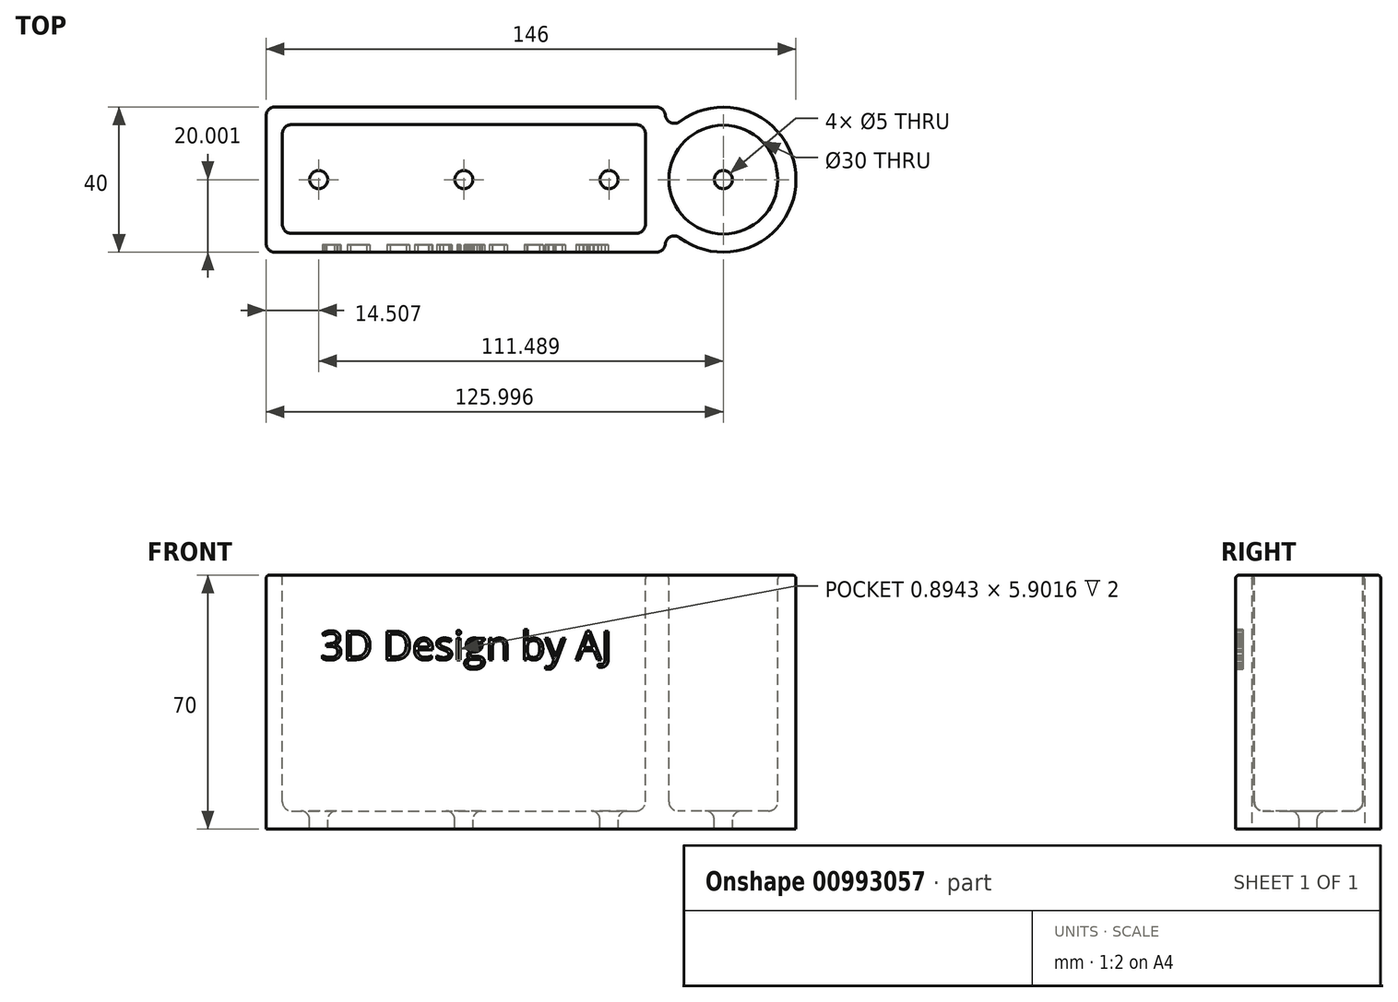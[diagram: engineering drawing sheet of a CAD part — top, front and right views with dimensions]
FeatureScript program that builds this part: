
annotation { "Feature Type Name" : "Feature", "Feature Type Description" : "" }
export const myFeature = defineFeature(function(context is Context, id is Id, definition is map)
    precondition{}
    {
        {
            var Q0;
            Q0=qCreatedBy(makeId("Top.planeOp"),FACE);
            var sketch = newSketch(context, id + "F0", { "sketchPlane" : qUnion([Q0])});
            skLineSegment(sketch, "E0.bottom", {"start": v(-60.33, 44.07) * mm, "end": v(49.67, 44.07) * mm});
            skLineSegment(sketch, "E0.top", {"start": v(-60.33, 4.07) * mm, "end": v(49.67, 4.07) * mm});
            skLineSegment(sketch, "E0.left", {"start": v(-60.33, 44.07) * mm, "end": v(-60.33, 4.07) * mm});
            skLineSegment(sketch, "E0.right", {"start": v(49.67, 44.07) * mm, "end": v(49.67, 4.07) * mm});
            skSolve(sketch);
        }
        {
            var Q0;
            Q0=makeQuery(id+"F0.imprint","IMPRINT",FACE,{"disambiguationData":[TD([[makeQuery(id+"F0.imprint","IMPRINT",EDGE,{"derivedFrom":sQuery(id+"F0.wireOp",EDGE,"E0.bottom")}),-1.0]])]});
            extrude(context, id + "F1", {"entities" : qUnion([Q0]), "depth" : 70 * mm, "offsetDistance" : 25 * mm});
        }
        {
            var Q0;
            Q0=makeQuery(id+"F1.opExtrude","CAP_FACE",FACE,{"disambiguationData":[OSD([sQuery(id+"F0.wireOp",EDGE,"E0.bottom"),sQuery(id+"F0.wireOp",EDGE,"E0.top"),sQuery(id+"F0.wireOp",EDGE,"E0.left"),sQuery(id+"F0.wireOp",EDGE,"E0.right")])],"isStart":false});
            var sketch = newSketch(context, id + "F2", { "sketchPlane" : qUnion([Q0])});
            skLineSegment(sketch, "E1.bottom", {"start": v(-55.82, 39.24) * mm, "end": v(44.18, 39.24) * mm});
            skLineSegment(sketch, "E1.top", {"start": v(-55.82, 9.24) * mm, "end": v(44.18, 9.24) * mm});
            skLineSegment(sketch, "E1.left", {"start": v(-55.82, 39.24) * mm, "end": v(-55.82, 9.24) * mm});
            skLineSegment(sketch, "E1.right", {"start": v(44.18, 39.24) * mm, "end": v(44.18, 9.24) * mm});
            skSolve(sketch);
        }
        {
            var Q0;
            Q0=makeQuery(id+"F2.imprint","IMPRINT",FACE,{"disambiguationData":[TD([[makeQuery(id+"F2.imprint","IMPRINT",EDGE,{"derivedFrom":sQuery(id+"F2.wireOp",EDGE,"E1.bottom")}),-1.0]])]});
            extrude(context, id + "F3", {"entities" : qUnion([Q0]), "operationType" : NewBodyOperationType.REMOVE, "oppositeDirection" : true, "depth" : 65 * mm, "offsetDistance" : 25 * mm});
        }
        {
            var Q0;
            Q0=qCreatedBy(makeId("Top.planeOp"),FACE);
            var sketch = newSketch(context, id + "F4", { "sketchPlane" : qUnion([Q0])});
            skCircle(sketch, "E2", {"center": v(65.67, 24.07) * mm, "radius": 20 * mm});
            skSolve(sketch);
        }
        {
            var Q0;
            Q0=makeQuery(id+"F4.imprint","IMPRINT",FACE,{"disambiguationData":[TD([[makeQuery(id+"F4.imprint","IMPRINT",EDGE,{"derivedFrom":sQuery(id+"F4.wireOp",EDGE,"E2")}),1.0]])]});
            extrude(context, id + "F5", {"entities" : qUnion([Q0]), "operationType" : NewBodyOperationType.ADD, "depth" : 70 * mm, "offsetDistance" : 25 * mm});
        }
        {
            var Q0;
            Q0=makeQuery(id+"F5.boolean.opBoolean","MERGE",FACE,{"derivedFrom":[makeQuery(id+"F1.opExtrude","CAP_FACE",FACE,{"disambiguationData":[OSD([sQuery(id+"F0.wireOp",EDGE,"E0.bottom"),sQuery(id+"F0.wireOp",EDGE,"E0.top"),sQuery(id+"F0.wireOp",EDGE,"E0.left"),sQuery(id+"F0.wireOp",EDGE,"E0.right")])],"isStart":false}),makeQuery(id+"F5.opExtrude","CAP_FACE",FACE,{"disambiguationData":[OSD([sQuery(id+"F4.wireOp",EDGE,"E2")])],"isStart":false})]});
            var sketch = newSketch(context, id + "F6", { "sketchPlane" : qUnion([Q0])});
            skCircle(sketch, "E3", {"center": v(65.67, 24.07) * mm, "radius": 15 * mm});
            skSolve(sketch);
        }
        {
            var Q0;
            Q0=makeQuery(id+"F6.imprint","IMPRINT",FACE,{"disambiguationData":[TD([[makeQuery(id+"F6.imprint","IMPRINT",EDGE,{"derivedFrom":sQuery(id+"F6.wireOp",EDGE,"E3")}),1.0]])]});
            extrude(context, id + "F7", {"entities" : qUnion([Q0]), "operationType" : NewBodyOperationType.REMOVE, "oppositeDirection" : true, "depth" : 65 * mm, "offsetDistance" : 25 * mm});
        }
        {
            var Q0;
            Q0=makeQuery(id+"F7.boolean.opBoolean","COPY",FACE,{"derivedFrom":makeQuery(id+"F7.opExtrude","CAP_FACE",FACE,{"disambiguationData":[OSD([sQuery(id+"F6.wireOp",EDGE,"E3")])],"isStart":false})});
            var sketch = newSketch(context, id + "F8", { "sketchPlane" : qUnion([Q0])});
            skLineSegment(sketch, "E4", {"start": v(65.67, 24.07) * mm, "end": v(34.18, 24.07) * mm});
            skLineSegment(sketch, "E5", {"start": v(34.18, 24.07) * mm, "end": v(-5.82, 24.07) * mm});
            skLineSegment(sketch, "E6", {"start": v(-5.82, 24.07) * mm, "end": v(-45.82, 24.07) * mm});
            skSolve(sketch);
        }
        {
            var Q0;
            Q0=sQuery(id+"F8.wireOp",VERTEX,"E6.end");
            var Q1;
            Q1=sQuery(id+"F8.wireOp",VERTEX,"E5.end");
            var Q2;
            Q2=sQuery(id+"F8.wireOp",VERTEX,"E4.end");
            var Q3;
            Q3=sQuery(id+"F8.wireOp",VERTEX,"E4.start");
            var Q4;
            Q4=makeQuery(id+"F1.opExtrude","SWEPT_BODY",BODY,{"disambiguationData":[OSD([sQuery(id+"F0.wireOp",EDGE,"E0.bottom"),sQuery(id+"F0.wireOp",EDGE,"E0.top"),sQuery(id+"F0.wireOp",EDGE,"E0.left"),sQuery(id+"F0.wireOp",EDGE,"E0.right")])]});
            hole(context, id + "F9", {"style" : HoleStyle.SIMPLE, "endStyle" : HoleEndStyle.THROUGH, "holeDiameter" : 5 * mm, "majorDiameter" : 5 * mm, "isTappedThrough" : true, "tappedDepth" : 12 * mm, "tapClearance" : 3, "locations" : qUnion([Q0, Q1, Q2, Q3]), "scope" : qUnion([Q4])});
        }
        {
            var Q0;
            Q0=makeQuery(id+"F3.boolean.opBoolean","COPY",EDGE,{"derivedFrom":makeQuery(id+"F3.opExtrude","SWEPT_EDGE",EDGE,{"disambiguationData":[OSD([sQuery(id+"F2.wireOp",EDGE,"E1.top"),sQuery(id+"F2.wireOp",EDGE,"E1.right")])]})});
            var Q1;
            Q1=makeQuery(id+"F3.boolean.opBoolean","COPY",EDGE,{"derivedFrom":makeQuery(id+"F3.opExtrude","SWEPT_EDGE",EDGE,{"disambiguationData":[OSD([sQuery(id+"F2.wireOp",EDGE,"E1.bottom"),sQuery(id+"F2.wireOp",EDGE,"E1.right")])]})});
            var Q2;
            Q2=makeQuery(id+"F3.boolean.opBoolean","COPY",EDGE,{"derivedFrom":makeQuery(id+"F3.opExtrude","SWEPT_EDGE",EDGE,{"disambiguationData":[OSD([sQuery(id+"F2.wireOp",EDGE,"E1.top"),sQuery(id+"F2.wireOp",EDGE,"E1.left")])]})});
            var Q3;
            Q3=makeQuery(id+"F3.boolean.opBoolean","COPY",EDGE,{"derivedFrom":makeQuery(id+"F3.opExtrude","SWEPT_EDGE",EDGE,{"disambiguationData":[OSD([sQuery(id+"F2.wireOp",EDGE,"E1.bottom"),sQuery(id+"F2.wireOp",EDGE,"E1.left")])]})});
            var Q4;
            Q4=makeQuery(id+"F5.boolean.opBoolean","INTERSECT",EDGE,{"disambiguationData":[OD(1.0)],"derivedFrom":[makeQuery(id+"F1.opExtrude","SWEPT_FACE",FACE,{"disambiguationData":[OSD([sQuery(id+"F0.wireOp",EDGE,"E0.right")])]}),makeQuery(id+"F5.opExtrude","SWEPT_FACE",FACE,{"disambiguationData":[OSD([sQuery(id+"F4.wireOp",EDGE,"E2")])]})]});
            var Q5;
            Q5=makeQuery(id+"F5.boolean.opBoolean","INTERSECT",EDGE,{"disambiguationData":[OD(0.0)],"derivedFrom":[makeQuery(id+"F1.opExtrude","SWEPT_FACE",FACE,{"disambiguationData":[OSD([sQuery(id+"F0.wireOp",EDGE,"E0.right")])]}),makeQuery(id+"F5.opExtrude","SWEPT_FACE",FACE,{"disambiguationData":[OSD([sQuery(id+"F4.wireOp",EDGE,"E2")])]})]});
            var Q6;
            Q6=makeQuery(id+"F3.boolean.opBoolean","COPY",EDGE,{"derivedFrom":makeQuery(id+"F3.opExtrude","CAP_EDGE",EDGE,{"disambiguationData":[OSD([sQuery(id+"F2.wireOp",EDGE,"E1.bottom")])],"isStart":false})});
            var Q7;
            Q7=makeQuery(id+"F3.boolean.opBoolean","COPY",FACE,{"derivedFrom":makeQuery(id+"F3.opExtrude","CAP_FACE",FACE,{"disambiguationData":[OSD([sQuery(id+"F2.wireOp",EDGE,"E1.bottom"),sQuery(id+"F2.wireOp",EDGE,"E1.top"),sQuery(id+"F2.wireOp",EDGE,"E1.left"),sQuery(id+"F2.wireOp",EDGE,"E1.right")])],"isStart":false})});
            fillet(context, id + "F10", {"entities" : qUnion([Q0, Q1, Q2, Q3, Q4, Q5, Q6, Q7]), "radius" : 2.5 * mm, "tangentPropagation" : true, "allowEdgeOverflow" : false});
        }
        {
            var Q0;
            Q0=makeQuery(id+"F7.boolean.opBoolean","COPY",FACE,{"derivedFrom":makeQuery(id+"F7.opExtrude","CAP_FACE",FACE,{"disambiguationData":[OSD([sQuery(id+"F6.wireOp",EDGE,"E3")])],"isStart":false})});
            fillet(context, id + "F11", {"entities" : qUnion([Q0]), "radius" : 2.5 * mm, "tangentPropagation" : true, "allowEdgeOverflow" : false});
        }
        {
            var Q0;
            Q0=makeQuery(id+"F5.boolean.opBoolean","MERGE",FACE,{"derivedFrom":[makeQuery(id+"F1.opExtrude","CAP_FACE",FACE,{"disambiguationData":[OSD([sQuery(id+"F0.wireOp",EDGE,"E0.bottom"),sQuery(id+"F0.wireOp",EDGE,"E0.top"),sQuery(id+"F0.wireOp",EDGE,"E0.left"),sQuery(id+"F0.wireOp",EDGE,"E0.right")])],"isStart":false}),makeQuery(id+"F5.opExtrude","CAP_FACE",FACE,{"disambiguationData":[OSD([sQuery(id+"F4.wireOp",EDGE,"E2")])],"isStart":false})]});
            fillet(context, id + "F12", {"entities" : qUnion([Q0]), "radius" : 1 * mm, "tangentPropagation" : true, "allowEdgeOverflow" : false});
        }
        {
            var Q0;
            Q0=makeQuery(id+"F1.opExtrude","SWEPT_EDGE",EDGE,{"disambiguationData":[OSD([sQuery(id+"F0.wireOp",EDGE,"E0.top"),sQuery(id+"F0.wireOp",EDGE,"E0.left")])]});
            var Q1;
            Q1=makeQuery(id+"F1.opExtrude","SWEPT_EDGE",EDGE,{"disambiguationData":[OSD([sQuery(id+"F0.wireOp",EDGE,"E0.bottom"),sQuery(id+"F0.wireOp",EDGE,"E0.left")])]});
            var Q2;
            Q2=makeQuery(id+"F1.opExtrude","SWEPT_EDGE",EDGE,{"disambiguationData":[OSD([sQuery(id+"F0.wireOp",EDGE,"E0.top"),sQuery(id+"F0.wireOp",EDGE,"E0.right")])]});
            var Q3;
            Q3=makeQuery(id+"F1.opExtrude","SWEPT_EDGE",EDGE,{"disambiguationData":[OSD([sQuery(id+"F0.wireOp",EDGE,"E0.bottom"),sQuery(id+"F0.wireOp",EDGE,"E0.right")])]});
            fillet(context, id + "F13", {"entities" : qUnion([Q0, Q1, Q2, Q3]), "radius" : 2.5 * mm, "tangentPropagation" : true, "allowEdgeOverflow" : false});
        }
        {
            var Q0;
            Q0=makeQuery(id+"F1.opExtrude","SWEPT_FACE",FACE,{"disambiguationData":[OSD([sQuery(id+"F0.wireOp",EDGE,"E0.top")])]});
            var sketch = newSketch(context, id + "F14", { "sketchPlane" : qUnion([Q0])});
            skText(sketch, "E7", { "text": "3D Design by AJ", "fontName": "OpenSans-Regular.ttf"});
            const initialGuessF14  = {"E7": [-0.04533, 0.04666, 1, 0, 0.00794]};
            skSetInitialGuess(sketch, initialGuessF14);
            skSolve(sketch);
        }
        {
            var Q0;
            Q0 = qSketchRegion(id + "F14", true);
            extrude(context, id + "F15", {"entities" : qUnion([Q0]), "operationType" : NewBodyOperationType.REMOVE, "oppositeDirection" : true, "depth" : 2 * mm, "offsetDistance" : 25 * mm});
        }
    });
